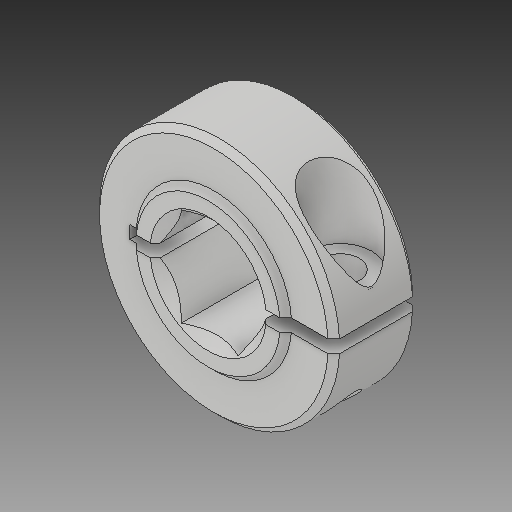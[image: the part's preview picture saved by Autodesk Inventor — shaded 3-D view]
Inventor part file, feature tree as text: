
AUTODESK INVENTOR PART (.ipt)
format: ipt  version: 2018 (Build 220112000, 112)  size: 184,320 bytes
history: native  units: in
note: dims shown in document units (in); Inventor stores cm internally (conversion verified against a paired STEP export)
features: mirror x1
ambient origin geometry x8: Origin, YZ Plane, XZ Plane, XY Plane, X Axis, Y Axis, Z Axis, Center Point
bodies: Solid1 (feature_tree)
feature tree (1):
  mirror  "Mirror2"
